# Revit family: Kitchen_Taps-Mixers_hansgrohe_72800CHN-Talis-M54-Single-lever-kitchen_new
name_source: partatom
category: Plumbing Fixtures
revit_build: Autodesk Revit 2018 (Build: 20170223_1515(x64)
units: mm (PartAtom-declared; Revit-internal decimal feet)

## family parameters
Always vertical = No
Cut with Voids When Loaded = No
OmniClass Number = 23.31.11.00
OmniClass Title = Faucets
Part Type = Normal
Room Calculation Point = No
Round Connector Dimension = Use Diameter
Shared = No
Work Plane-Based = Yes

## types (2) — shared parameters
Always visible = Yes
BIMobject category = Taps & Mixers
Connector Description = Water Inlet 12.7mm
Default Elevation = 1219.2 mm  [stored 4 ft]
Description = Talis M54 Single lever kitchen mixer 210, pull-out spray, 2jet
Diameter = 13 mm
Edition number = 1
IFC Classification = Valve
Manufacturer = Hansgrohe
Manufacturer name = hansgrohe
Model = 72800CHN
OmniClass Code = 23-31 11 00
OmniClass Description = Faucets
Product Guid = ff16b898-9eb0-4849-897e-1e7dfe319b2a
Product SKU = 72800CHN
Product data url = https://bimobject.com
Product family = Talis M54
Product group = Kitchen mixers
Product name = 72800CHN Talis M54 Single lever kitchen mixer 210, pull-out spray, 2jet
Product url = https://www.hansgrohe.com
QR code = https://bimobject.com
URL = https://www.hansgrohe.com
Weight Net (Kg) = 2.6

## per-type parameters (varying)
| type | Material 1 |
| 677 Matt Black | Hansgrohe - Metal - 677 Matt Black |
| 007 Chrome | Hansgrohe - Metal - 007 Chrome |

note: [stored X ft] marks values corroborated as IEEE doubles in the binary element streams (Revit-internal decimal feet)

## geometry (parser evidence)
native form markers: Sweep x3
no freeform markers — native parametric forms only
